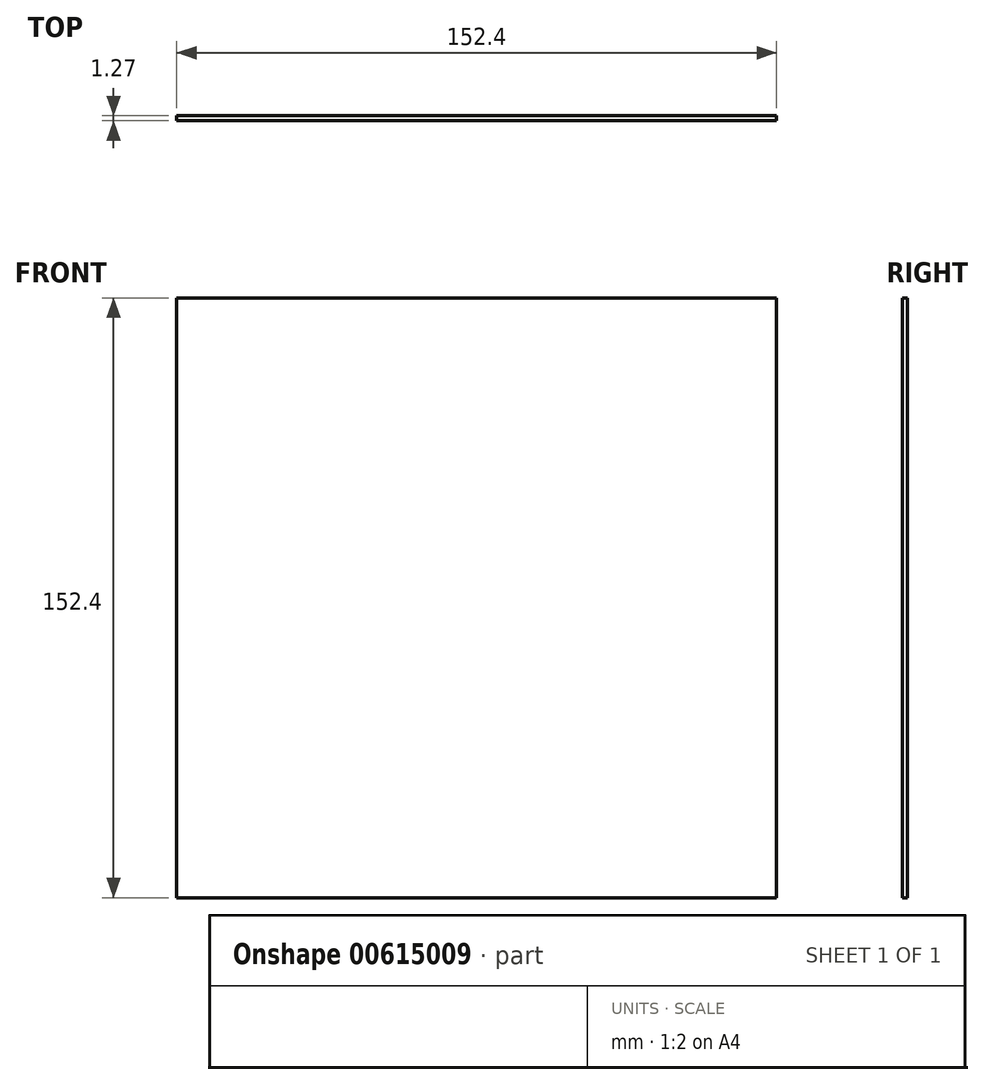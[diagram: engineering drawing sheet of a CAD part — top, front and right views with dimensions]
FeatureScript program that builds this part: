
annotation { "Feature Type Name" : "Feature", "Feature Type Description" : "" }
export const myFeature = defineFeature(function(context is Context, id is Id, definition is map)
    precondition{}
    {
        {
            var Q0;
            Q0=qCreatedBy(makeId("Front.planeOp"),FACE);
            var sketch = newSketch(context, id + "F0", { "sketchPlane" : qUnion([Q0])});
            skLineSegment(sketch, "E0.bottom", {"start": v(76.2, -76.2) * mm, "end": v(-76.2, -76.2) * mm});
            skLineSegment(sketch, "E0.top", {"start": v(76.2, 76.2) * mm, "end": v(-76.2, 76.2) * mm});
            skLineSegment(sketch, "E0.left", {"start": v(76.2, -76.2) * mm, "end": v(76.2, 76.2) * mm});
            skLineSegment(sketch, "E0.right", {"start": v(-76.2, -76.2) * mm, "end": v(-76.2, 76.2) * mm});
            skPoint(sketch, "E0.middle", {"position": v(0, 0) * mm});
            skSolve(sketch);
        }
        {
            var Q0;
            Q0 = qSketchRegion(id + "F0", true);
            extrude(context, id + "F1", {"entities" : qUnion([Q0]), "depth" : 1.27 * mm, "offsetDistance" : 25.4 * mm});
        }
    });
